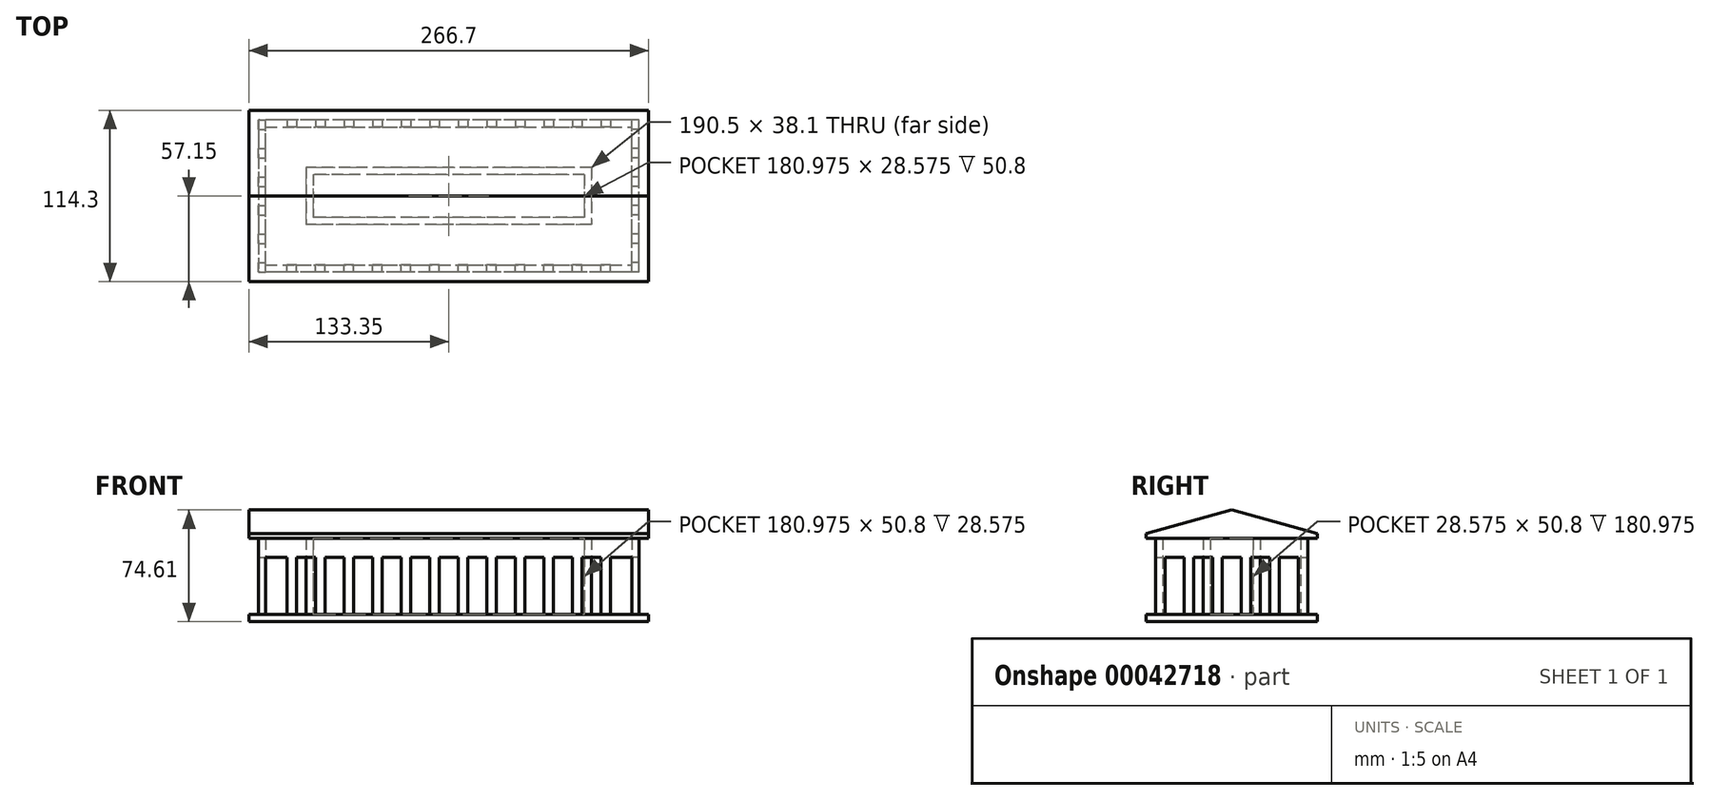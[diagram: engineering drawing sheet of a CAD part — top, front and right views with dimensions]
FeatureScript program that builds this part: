
annotation { "Feature Type Name" : "Feature", "Feature Type Description" : "" }
export const myFeature = defineFeature(function(context is Context, id is Id, definition is map)
    precondition{}
    {
        {
            var Q0;
            Q0=qCreatedBy(makeId("Top.planeOp"),FACE);
            var sketch = newSketch(context, id + "F0", { "sketchPlane" : qUnion([Q0])});
            skLineSegment(sketch, "E0.rect.bottom", {"start": v(133.35, 57.15) * mm, "end": v(-133.35, 57.15) * mm});
            skLineSegment(sketch, "E0.rect.top", {"start": v(133.35, -57.15) * mm, "end": v(-133.35, -57.15) * mm});
            skLineSegment(sketch, "E0.rect.left", {"start": v(133.35, 57.15) * mm, "end": v(133.35, -57.15) * mm});
            skLineSegment(sketch, "E0.rect.right", {"start": v(-133.35, 57.15) * mm, "end": v(-133.35, -57.15) * mm});
            skPoint(sketch, "E0.rect.middle", {"position": v(0, 0) * mm});
            skSolve(sketch);
        }
        {
            var Q0;
            Q0 = qSketchRegion(id + "F0", true);
            extrude(context, id + "F1", {"entities" : qUnion([Q0]), "depth" : 4.76 * mm});
        }
        {
            var Q0;
            Q0=makeQuery(id+"F1.opExtrude","CAP_FACE",FACE,{"disambiguationData":[OSD([sQuery(id+"F0.wireOp",EDGE,"E0.rect.bottom"),sQuery(id+"F0.wireOp",EDGE,"E0.rect.top"),sQuery(id+"F0.wireOp",EDGE,"E0.rect.left"),sQuery(id+"F0.wireOp",EDGE,"E0.rect.right")])],"isStart":false});
            var sketch = newSketch(context, id + "F2", { "sketchPlane" : qUnion([Q0])});
            skLineSegment(sketch, "E1.bottom", {"start": v(127, -50.8) * mm, "end": v(122.24, -50.8) * mm});
            skLineSegment(sketch, "E1.top", {"start": v(127, -44.45) * mm, "end": v(122.24, -44.45) * mm});
            skLineSegment(sketch, "E1.left", {"start": v(127, -50.8) * mm, "end": v(127, -44.45) * mm});
            skLineSegment(sketch, "E1.right", {"start": v(122.24, -50.8) * mm, "end": v(122.24, -44.45) * mm});
            skLineSegment(sketch, "E2.0.1.0", {"start": v(127, -25.4) * mm, "end": v(122.24, -25.4) * mm});
            skLineSegment(sketch, "E2.0.1.1", {"start": v(122.24, -31.75) * mm, "end": v(122.24, -25.4) * mm});
            skLineSegment(sketch, "E2.0.1.2", {"start": v(127, -31.75) * mm, "end": v(127, -25.4) * mm});
            skLineSegment(sketch, "E2.0.1.3", {"start": v(127, -31.75) * mm, "end": v(122.24, -31.75) * mm});
            skLineSegment(sketch, "E2.0.2.0", {"start": v(127, -6.35) * mm, "end": v(122.24, -6.35) * mm});
            skLineSegment(sketch, "E2.0.2.1", {"start": v(122.24, -12.7) * mm, "end": v(122.24, -6.35) * mm});
            skLineSegment(sketch, "E2.0.2.2", {"start": v(127, -12.7) * mm, "end": v(127, -6.35) * mm});
            skLineSegment(sketch, "E2.0.2.3", {"start": v(127, -12.7) * mm, "end": v(122.24, -12.7) * mm});
            skLineSegment(sketch, "E2.0.3.0", {"start": v(127, 12.7) * mm, "end": v(122.24, 12.7) * mm});
            skLineSegment(sketch, "E2.0.3.1", {"start": v(122.24, 6.35) * mm, "end": v(122.24, 12.7) * mm});
            skLineSegment(sketch, "E2.0.3.2", {"start": v(127, 6.35) * mm, "end": v(127, 12.7) * mm});
            skLineSegment(sketch, "E2.0.3.3", {"start": v(127, 6.35) * mm, "end": v(122.24, 6.35) * mm});
            skLineSegment(sketch, "E2.0.4.0", {"start": v(127, 31.75) * mm, "end": v(122.24, 31.75) * mm});
            skLineSegment(sketch, "E2.0.4.1", {"start": v(122.24, 25.4) * mm, "end": v(122.24, 31.75) * mm});
            skLineSegment(sketch, "E2.0.4.2", {"start": v(127, 25.4) * mm, "end": v(127, 31.75) * mm});
            skLineSegment(sketch, "E2.0.4.3", {"start": v(127, 25.4) * mm, "end": v(122.24, 25.4) * mm});
            skLineSegment(sketch, "E2.direction1", {"start": v(122.24, -44.45) * mm, "end": v(149.23, -44.45) * mm, "construction": true});
            skLineSegment(sketch, "E2.direction2", {"start": v(122.24, -44.45) * mm, "end": v(122.24, -25.4) * mm, "construction": true});
            skLineSegment(sketch, "E3.0.0.5", {"start": v(127, 50.8) * mm, "end": v(122.24, 50.8) * mm});
            skLineSegment(sketch, "E3.3.0.5", {"start": v(122.24, 44.45) * mm, "end": v(122.24, 50.8) * mm});
            skLineSegment(sketch, "E3.6.0.5", {"start": v(127, 44.45) * mm, "end": v(127, 50.8) * mm});
            skLineSegment(sketch, "E3.9.0.5", {"start": v(127, 44.45) * mm, "end": v(122.24, 44.45) * mm});
            skLineSegment(sketch, "E4.bottom", {"start": v(107.95, 50.8) * mm, "end": v(101.6, 50.8) * mm});
            skLineSegment(sketch, "E4.top", {"start": v(107.95, 46.04) * mm, "end": v(101.6, 46.04) * mm});
            skLineSegment(sketch, "E4.left", {"start": v(107.95, 50.8) * mm, "end": v(107.95, 46.04) * mm});
            skLineSegment(sketch, "E4.right", {"start": v(101.6, 50.8) * mm, "end": v(101.6, 46.04) * mm});
            skLineSegment(sketch, "E5", {"start": v(0, -57.15) * mm, "end": v(0, 57.15) * mm, "construction": true});
            skLineSegment(sketch, "E6.MirrorCS", {"start": v(-127, -44.45) * mm, "end": v(-122.24, -44.45) * mm});
            skLineSegment(sketch, "E7.MirrorCS", {"start": v(-127, -31.75) * mm, "end": v(-122.24, -31.75) * mm});
            skLineSegment(sketch, "E8.MirrorCS", {"start": v(-127, -25.4) * mm, "end": v(-122.24, -25.4) * mm});
            skLineSegment(sketch, "E9.MirrorCS", {"start": v(-127, -6.35) * mm, "end": v(-122.24, -6.35) * mm});
            skLineSegment(sketch, "E10.MirrorCS", {"start": v(-127, -31.75) * mm, "end": v(-127, -25.4) * mm});
            skLineSegment(sketch, "E11.MirrorCS", {"start": v(-122.24, -31.75) * mm, "end": v(-122.24, -25.4) * mm});
            skLineSegment(sketch, "E12.MirrorCS", {"start": v(-122.24, -50.8) * mm, "end": v(-122.24, -44.45) * mm});
            skLineSegment(sketch, "E13.MirrorCS", {"start": v(-127, -50.8) * mm, "end": v(-127, -44.45) * mm});
            skLineSegment(sketch, "E14.MirrorCS", {"start": v(-127, -50.8) * mm, "end": v(-122.24, -50.8) * mm});
            skLineSegment(sketch, "E15.MirrorCS", {"start": v(-127, 6.35) * mm, "end": v(-122.24, 6.35) * mm});
            skLineSegment(sketch, "E16.MirrorCS", {"start": v(-127, 6.35) * mm, "end": v(-127, 12.7) * mm});
            skLineSegment(sketch, "E17.MirrorCS", {"start": v(-122.24, 6.35) * mm, "end": v(-122.24, 12.7) * mm});
            skLineSegment(sketch, "E18.MirrorCS", {"start": v(-122.24, -12.7) * mm, "end": v(-122.24, -6.35) * mm});
            skLineSegment(sketch, "E19.MirrorCS", {"start": v(-127, -12.7) * mm, "end": v(-127, -6.35) * mm});
            skLineSegment(sketch, "E20.MirrorCS", {"start": v(-127, -12.7) * mm, "end": v(-122.24, -12.7) * mm});
            skLineSegment(sketch, "E21.MirrorCS", {"start": v(-122.24, 25.4) * mm, "end": v(-122.24, 31.75) * mm});
            skLineSegment(sketch, "E22.MirrorCS", {"start": v(-127, 44.45) * mm, "end": v(-127, 50.8) * mm});
            skLineSegment(sketch, "E23.MirrorCS", {"start": v(-127, 12.7) * mm, "end": v(-122.24, 12.7) * mm});
            skLineSegment(sketch, "E24.MirrorCS", {"start": v(-127, 25.4) * mm, "end": v(-122.24, 25.4) * mm});
            skLineSegment(sketch, "E25.MirrorCS", {"start": v(-127, 31.75) * mm, "end": v(-122.24, 31.75) * mm});
            skLineSegment(sketch, "E26.MirrorCS", {"start": v(-127, 25.4) * mm, "end": v(-127, 31.75) * mm});
            skLineSegment(sketch, "E27.MirrorCS", {"start": v(-127, 50.8) * mm, "end": v(-122.24, 50.8) * mm});
            skLineSegment(sketch, "E28.MirrorCS", {"start": v(-127, 44.45) * mm, "end": v(-122.24, 44.45) * mm});
            skLineSegment(sketch, "E29.MirrorCS", {"start": v(-122.24, 44.45) * mm, "end": v(-122.24, 50.8) * mm});
            skLineSegment(sketch, "E30.0.0", {"start": v(133.35, 57.15) * mm, "end": v(-133.35, 57.15) * mm});
            skLineSegment(sketch, "E30.0.2", {"start": v(-133.35, 57.15) * mm, "end": v(133.35, 57.15) * mm});
            skLineSegment(sketch, "E31.0.0", {"start": v(133.35, -57.15) * mm, "end": v(133.35, 57.15) * mm});
            skLineSegment(sketch, "E31.0.2", {"start": v(-133.35, 57.15) * mm, "end": v(-133.35, -57.15) * mm});
            skLineSegment(sketch, "E31.0.3", {"start": v(-133.35, -57.15) * mm, "end": v(133.35, -57.15) * mm});
            skLineSegment(sketch, "E32.1.0.0", {"start": v(88.9, 50.8) * mm, "end": v(82.55, 50.8) * mm});
            skLineSegment(sketch, "E32.1.0.1", {"start": v(88.9, 46.04) * mm, "end": v(82.55, 46.04) * mm});
            skLineSegment(sketch, "E32.1.0.2", {"start": v(88.9, 50.8) * mm, "end": v(88.9, 46.04) * mm});
            skLineSegment(sketch, "E32.1.0.3", {"start": v(82.55, 50.8) * mm, "end": v(82.55, 46.04) * mm});
            skLineSegment(sketch, "E32.2.0.0", {"start": v(69.85, 50.8) * mm, "end": v(63.5, 50.8) * mm});
            skLineSegment(sketch, "E32.2.0.1", {"start": v(69.85, 46.04) * mm, "end": v(63.5, 46.04) * mm});
            skLineSegment(sketch, "E32.2.0.2", {"start": v(69.85, 50.8) * mm, "end": v(69.85, 46.04) * mm});
            skLineSegment(sketch, "E32.2.0.3", {"start": v(63.5, 50.8) * mm, "end": v(63.5, 46.04) * mm});
            skLineSegment(sketch, "E32.3.0.0", {"start": v(50.8, 50.8) * mm, "end": v(44.45, 50.8) * mm});
            skLineSegment(sketch, "E32.3.0.1", {"start": v(50.8, 46.04) * mm, "end": v(44.45, 46.04) * mm});
            skLineSegment(sketch, "E32.3.0.2", {"start": v(50.8, 50.8) * mm, "end": v(50.8, 46.04) * mm});
            skLineSegment(sketch, "E32.3.0.3", {"start": v(44.45, 50.8) * mm, "end": v(44.45, 46.04) * mm});
            skLineSegment(sketch, "E32.4.0.0", {"start": v(31.75, 50.8) * mm, "end": v(25.4, 50.8) * mm});
            skLineSegment(sketch, "E32.4.0.1", {"start": v(31.75, 46.04) * mm, "end": v(25.4, 46.04) * mm});
            skLineSegment(sketch, "E32.4.0.2", {"start": v(31.75, 50.8) * mm, "end": v(31.75, 46.04) * mm});
            skLineSegment(sketch, "E32.4.0.3", {"start": v(25.4, 50.8) * mm, "end": v(25.4, 46.04) * mm});
            skLineSegment(sketch, "E32.5.0.0", {"start": v(12.7, 50.8) * mm, "end": v(6.35, 50.8) * mm});
            skLineSegment(sketch, "E32.5.0.1", {"start": v(12.7, 46.04) * mm, "end": v(6.35, 46.04) * mm});
            skLineSegment(sketch, "E32.5.0.2", {"start": v(12.7, 50.8) * mm, "end": v(12.7, 46.04) * mm});
            skLineSegment(sketch, "E32.5.0.3", {"start": v(6.35, 50.8) * mm, "end": v(6.35, 46.04) * mm});
            skLineSegment(sketch, "E32.6.0.0", {"start": v(-6.35, 50.8) * mm, "end": v(-12.7, 50.8) * mm});
            skLineSegment(sketch, "E32.6.0.1", {"start": v(-6.35, 46.04) * mm, "end": v(-12.7, 46.04) * mm});
            skLineSegment(sketch, "E32.6.0.2", {"start": v(-6.35, 50.8) * mm, "end": v(-6.35, 46.04) * mm});
            skLineSegment(sketch, "E32.6.0.3", {"start": v(-12.7, 50.8) * mm, "end": v(-12.7, 46.04) * mm});
            skLineSegment(sketch, "E32.7.0.0", {"start": v(-25.4, 50.8) * mm, "end": v(-31.75, 50.8) * mm});
            skLineSegment(sketch, "E32.7.0.1", {"start": v(-25.4, 46.04) * mm, "end": v(-31.75, 46.04) * mm});
            skLineSegment(sketch, "E32.7.0.2", {"start": v(-25.4, 50.8) * mm, "end": v(-25.4, 46.04) * mm});
            skLineSegment(sketch, "E32.7.0.3", {"start": v(-31.75, 50.8) * mm, "end": v(-31.75, 46.04) * mm});
            skLineSegment(sketch, "E32.8.0.0", {"start": v(-44.45, 50.8) * mm, "end": v(-50.8, 50.8) * mm});
            skLineSegment(sketch, "E32.8.0.1", {"start": v(-44.45, 46.04) * mm, "end": v(-50.8, 46.04) * mm});
            skLineSegment(sketch, "E32.8.0.2", {"start": v(-44.45, 50.8) * mm, "end": v(-44.45, 46.04) * mm});
            skLineSegment(sketch, "E32.8.0.3", {"start": v(-50.8, 50.8) * mm, "end": v(-50.8, 46.04) * mm});
            skLineSegment(sketch, "E32.9.0.0", {"start": v(-63.5, 50.8) * mm, "end": v(-69.85, 50.8) * mm});
            skLineSegment(sketch, "E32.9.0.1", {"start": v(-63.5, 46.04) * mm, "end": v(-69.85, 46.04) * mm});
            skLineSegment(sketch, "E32.9.0.2", {"start": v(-63.5, 50.8) * mm, "end": v(-63.5, 46.04) * mm});
            skLineSegment(sketch, "E32.9.0.3", {"start": v(-69.85, 50.8) * mm, "end": v(-69.85, 46.04) * mm});
            skLineSegment(sketch, "E32.10.0.0", {"start": v(-82.55, 50.8) * mm, "end": v(-88.9, 50.8) * mm});
            skLineSegment(sketch, "E32.10.0.1", {"start": v(-82.55, 46.04) * mm, "end": v(-88.9, 46.04) * mm});
            skLineSegment(sketch, "E32.10.0.2", {"start": v(-82.55, 50.8) * mm, "end": v(-82.55, 46.04) * mm});
            skLineSegment(sketch, "E32.10.0.3", {"start": v(-88.9, 50.8) * mm, "end": v(-88.9, 46.04) * mm});
            skLineSegment(sketch, "E32.direction1", {"start": v(101.6, 50.8) * mm, "end": v(82.55, 50.8) * mm, "construction": true});
            skLineSegment(sketch, "E33.0.11.0", {"start": v(-101.6, 50.8) * mm, "end": v(-107.95, 50.8) * mm});
            skLineSegment(sketch, "E33.3.11.0", {"start": v(-101.6, 46.04) * mm, "end": v(-107.95, 46.04) * mm});
            skLineSegment(sketch, "E33.6.11.0", {"start": v(-101.6, 50.8) * mm, "end": v(-101.6, 46.04) * mm});
            skLineSegment(sketch, "E33.9.11.0", {"start": v(-107.95, 50.8) * mm, "end": v(-107.95, 46.04) * mm});
            skLineSegment(sketch, "E34", {"start": v(133.35, 0) * mm, "end": v(-133.35, 0) * mm, "construction": true});
            skLineSegment(sketch, "E35.MirrorCS", {"start": v(107.95, -50.8) * mm, "end": v(107.95, -46.04) * mm});
            skLineSegment(sketch, "E36.MirrorCS", {"start": v(107.95, -46.04) * mm, "end": v(101.6, -46.04) * mm});
            skLineSegment(sketch, "E37.MirrorCS", {"start": v(107.95, -50.8) * mm, "end": v(101.6, -50.8) * mm});
            skLineSegment(sketch, "E38.MirrorCS", {"start": v(101.6, -50.8) * mm, "end": v(101.6, -46.04) * mm});
            skLineSegment(sketch, "E39.MirrorCS", {"start": v(88.9, -50.8) * mm, "end": v(88.9, -46.04) * mm});
            skLineSegment(sketch, "E40.MirrorCS", {"start": v(88.9, -46.04) * mm, "end": v(82.55, -46.04) * mm});
            skLineSegment(sketch, "E41.MirrorCS", {"start": v(82.55, -50.8) * mm, "end": v(82.55, -46.04) * mm});
            skLineSegment(sketch, "E42.MirrorCS", {"start": v(88.9, -50.8) * mm, "end": v(82.55, -50.8) * mm});
            skLineSegment(sketch, "E43.MirrorCS", {"start": v(69.85, -50.8) * mm, "end": v(69.85, -46.04) * mm});
            skLineSegment(sketch, "E44.MirrorCS", {"start": v(-6.35, -50.8) * mm, "end": v(-6.35, -46.04) * mm});
            skLineSegment(sketch, "E45.MirrorCS", {"start": v(-82.55, -50.8) * mm, "end": v(-82.55, -46.04) * mm});
            skLineSegment(sketch, "E46.MirrorCS", {"start": v(-44.45, -46.04) * mm, "end": v(-50.8, -46.04) * mm});
            skLineSegment(sketch, "E47.MirrorCS", {"start": v(31.75, -46.04) * mm, "end": v(25.4, -46.04) * mm});
            skLineSegment(sketch, "E48.MirrorCS", {"start": v(69.85, -46.04) * mm, "end": v(63.5, -46.04) * mm});
            skLineSegment(sketch, "E49.MirrorCS", {"start": v(-6.35, -46.04) * mm, "end": v(-12.7, -46.04) * mm});
            skLineSegment(sketch, "E50.MirrorCS", {"start": v(-82.55, -46.04) * mm, "end": v(-88.9, -46.04) * mm});
            skLineSegment(sketch, "E51.MirrorCS", {"start": v(-44.45, -50.8) * mm, "end": v(-50.8, -50.8) * mm});
            skLineSegment(sketch, "E52.MirrorCS", {"start": v(-107.95, -50.8) * mm, "end": v(-107.95, -46.04) * mm});
            skLineSegment(sketch, "E53.MirrorCS", {"start": v(31.75, -50.8) * mm, "end": v(25.4, -50.8) * mm});
            skLineSegment(sketch, "E54.MirrorCS", {"start": v(69.85, -50.8) * mm, "end": v(63.5, -50.8) * mm});
            skLineSegment(sketch, "E55.MirrorCS", {"start": v(-6.35, -50.8) * mm, "end": v(-12.7, -50.8) * mm});
            skLineSegment(sketch, "E56.MirrorCS", {"start": v(-82.55, -50.8) * mm, "end": v(-88.9, -50.8) * mm});
            skLineSegment(sketch, "E57.MirrorCS", {"start": v(-31.75, -50.8) * mm, "end": v(-31.75, -46.04) * mm});
            skLineSegment(sketch, "E58.MirrorCS", {"start": v(-101.6, -50.8) * mm, "end": v(-101.6, -46.04) * mm});
            skLineSegment(sketch, "E59.MirrorCS", {"start": v(44.45, -50.8) * mm, "end": v(44.45, -46.04) * mm});
            skLineSegment(sketch, "E60.MirrorCS", {"start": v(-25.4, -50.8) * mm, "end": v(-25.4, -46.04) * mm});
            skLineSegment(sketch, "E61.MirrorCS", {"start": v(-101.6, -46.04) * mm, "end": v(-107.95, -46.04) * mm});
            skLineSegment(sketch, "E62.MirrorCS", {"start": v(50.8, -50.8) * mm, "end": v(50.8, -46.04) * mm});
            skLineSegment(sketch, "E63.MirrorCS", {"start": v(6.35, -50.8) * mm, "end": v(6.35, -46.04) * mm});
            skLineSegment(sketch, "E64.MirrorCS", {"start": v(-69.85, -50.8) * mm, "end": v(-69.85, -46.04) * mm});
            skLineSegment(sketch, "E65.MirrorCS", {"start": v(50.8, -46.04) * mm, "end": v(44.45, -46.04) * mm});
            skLineSegment(sketch, "E66.MirrorCS", {"start": v(-25.4, -46.04) * mm, "end": v(-31.75, -46.04) * mm});
            skLineSegment(sketch, "E67.MirrorCS", {"start": v(12.7, -50.8) * mm, "end": v(12.7, -46.04) * mm});
            skLineSegment(sketch, "E68.MirrorCS", {"start": v(-63.5, -50.8) * mm, "end": v(-63.5, -46.04) * mm});
            skLineSegment(sketch, "E69.MirrorCS", {"start": v(-101.6, -50.8) * mm, "end": v(-107.95, -50.8) * mm});
            skLineSegment(sketch, "E70.MirrorCS", {"start": v(50.8, -50.8) * mm, "end": v(44.45, -50.8) * mm});
            skLineSegment(sketch, "E71.MirrorCS", {"start": v(12.7, -46.04) * mm, "end": v(6.35, -46.04) * mm});
            skLineSegment(sketch, "E72.MirrorCS", {"start": v(-25.4, -50.8) * mm, "end": v(-31.75, -50.8) * mm});
            skLineSegment(sketch, "E73.MirrorCS", {"start": v(-63.5, -46.04) * mm, "end": v(-69.85, -46.04) * mm});
            skLineSegment(sketch, "E74.MirrorCS", {"start": v(-50.8, -50.8) * mm, "end": v(-50.8, -46.04) * mm});
            skLineSegment(sketch, "E75.MirrorCS", {"start": v(25.4, -50.8) * mm, "end": v(25.4, -46.04) * mm});
            skLineSegment(sketch, "E76.MirrorCS", {"start": v(63.5, -50.8) * mm, "end": v(63.5, -46.04) * mm});
            skLineSegment(sketch, "E77.MirrorCS", {"start": v(-12.7, -50.8) * mm, "end": v(-12.7, -46.04) * mm});
            skLineSegment(sketch, "E78.MirrorCS", {"start": v(-63.5, -50.8) * mm, "end": v(-69.85, -50.8) * mm});
            skLineSegment(sketch, "E79.MirrorCS", {"start": v(12.7, -50.8) * mm, "end": v(6.35, -50.8) * mm});
            skLineSegment(sketch, "E80.MirrorCS", {"start": v(31.75, -50.8) * mm, "end": v(31.75, -46.04) * mm});
            skLineSegment(sketch, "E81.MirrorCS", {"start": v(-88.9, -50.8) * mm, "end": v(-88.9, -46.04) * mm});
            skLineSegment(sketch, "E82.MirrorCS", {"start": v(-44.45, -50.8) * mm, "end": v(-44.45, -46.04) * mm});
            skSolve(sketch);
        }
        {
            var Q0;
            Q0=makeQuery(id+"F2.imprint","IMPRINT",FACE,{"disambiguationData":[TD([[makeQuery(id+"F2.imprint","IMPRINT",EDGE,{"derivedFrom":sQuery(id+"F2.wireOp",EDGE,"E1.bottom")}),-1.0]])]});
            var Q1;
            Q1=makeQuery(id+"F2.imprint","IMPRINT",FACE,{"disambiguationData":[TD([[makeQuery(id+"F2.imprint","IMPRINT",EDGE,{"derivedFrom":sQuery(id+"F2.wireOp",EDGE,"E2.0.3.0")}),1.0]])]});
            var Q2;
            {var subQ5=sQuery(id+"F2.wireOp",EDGE,"E2.0.4.0");Q2=makeQuery(id+"F2.imprint","IMPRINT",FACE,{"disambiguationData":[TD([[makeQuery(id+"F2.imprint","IMPRINT",EDGE,{"derivedFrom":subQ5}),1.0]])]});}
            var Q3;
            {var subQ5=sQuery(id+"F2.wireOp",EDGE,"E2.0.4.3");Q3=makeQuery(id+"F2.imprint","IMPRINT",FACE,{"disambiguationData":[TD([[makeQuery(id+"F2.imprint","IMPRINT",EDGE,{"derivedFrom":subQ5}),-1.0]])]});}
            var Q4;
            Q4=makeQuery(id+"F2.imprint","IMPRINT",FACE,{"disambiguationData":[TD([[makeQuery(id+"F2.imprint","IMPRINT",EDGE,{"derivedFrom":sQuery(id+"F2.wireOp",EDGE,"E2.0.2.0")}),1.0]])]});
            var Q5;
            Q5=makeQuery(id+"F2.imprint","IMPRINT",FACE,{"disambiguationData":[TD([[makeQuery(id+"F2.imprint","IMPRINT",EDGE,{"derivedFrom":sQuery(id+"F2.wireOp",EDGE,"E2.0.1.0")}),1.0]])]});
            var Q6;
            Q6=makeQuery(id+"F2.imprint","IMPRINT",FACE,{"disambiguationData":[TD([[makeQuery(id+"F2.imprint","IMPRINT",EDGE,{"derivedFrom":sQuery(id+"F2.wireOp",EDGE,"E22.MirrorCS")}),-1.0]])]});
            var Q7;
            Q7=makeQuery(id+"F2.imprint","IMPRINT",FACE,{"disambiguationData":[TD([[makeQuery(id+"F2.imprint","IMPRINT",EDGE,{"derivedFrom":sQuery(id+"F2.wireOp",EDGE,"E33.0.11.0")}),1.0]])]});
            var Q8;
            Q8=makeQuery(id+"F2.imprint","IMPRINT",FACE,{"disambiguationData":[TD([[makeQuery(id+"F2.imprint","IMPRINT",EDGE,{"derivedFrom":sQuery(id+"F2.wireOp",EDGE,"E32.10.0.0")}),1.0]])]});
            var Q9;
            Q9=makeQuery(id+"F2.imprint","IMPRINT",FACE,{"disambiguationData":[TD([[makeQuery(id+"F2.imprint","IMPRINT",EDGE,{"derivedFrom":sQuery(id+"F2.wireOp",EDGE,"E32.9.0.0")}),1.0]])]});
            var Q10;
            Q10=makeQuery(id+"F2.imprint","IMPRINT",FACE,{"disambiguationData":[TD([[makeQuery(id+"F2.imprint","IMPRINT",EDGE,{"derivedFrom":sQuery(id+"F2.wireOp",EDGE,"E32.8.0.0")}),1.0]])]});
            var Q11;
            Q11=makeQuery(id+"F2.imprint","IMPRINT",FACE,{"disambiguationData":[TD([[makeQuery(id+"F2.imprint","IMPRINT",EDGE,{"derivedFrom":sQuery(id+"F2.wireOp",EDGE,"E32.7.0.0")}),1.0]])]});
            var Q12;
            Q12=makeQuery(id+"F2.imprint","IMPRINT",FACE,{"disambiguationData":[TD([[makeQuery(id+"F2.imprint","IMPRINT",EDGE,{"derivedFrom":sQuery(id+"F2.wireOp",EDGE,"E32.5.0.0")}),1.0]])]});
            var Q13;
            Q13=makeQuery(id+"F2.imprint","IMPRINT",FACE,{"disambiguationData":[TD([[makeQuery(id+"F2.imprint","IMPRINT",EDGE,{"derivedFrom":sQuery(id+"F2.wireOp",EDGE,"E32.4.0.0")}),1.0]])]});
            var Q14;
            Q14=makeQuery(id+"F2.imprint","IMPRINT",FACE,{"disambiguationData":[TD([[makeQuery(id+"F2.imprint","IMPRINT",EDGE,{"derivedFrom":sQuery(id+"F2.wireOp",EDGE,"E32.3.0.0")}),1.0]])]});
            var Q15;
            Q15=makeQuery(id+"F2.imprint","IMPRINT",FACE,{"disambiguationData":[TD([[makeQuery(id+"F2.imprint","IMPRINT",EDGE,{"derivedFrom":sQuery(id+"F2.wireOp",EDGE,"E32.2.0.0")}),1.0]])]});
            var Q16;
            Q16=makeQuery(id+"F2.imprint","IMPRINT",FACE,{"disambiguationData":[TD([[makeQuery(id+"F2.imprint","IMPRINT",EDGE,{"derivedFrom":sQuery(id+"F2.wireOp",EDGE,"E32.1.0.0")}),1.0]])]});
            var Q17;
            Q17=makeQuery(id+"F2.imprint","IMPRINT",FACE,{"disambiguationData":[TD([[makeQuery(id+"F2.imprint","IMPRINT",EDGE,{"derivedFrom":sQuery(id+"F2.wireOp",EDGE,"E4.bottom")}),1.0]])]});
            var Q18;
            Q18=makeQuery(id+"F2.imprint","IMPRINT",FACE,{"disambiguationData":[TD([[makeQuery(id+"F2.imprint","IMPRINT",EDGE,{"derivedFrom":sQuery(id+"F2.wireOp",EDGE,"E3.0.0.5")}),1.0]])]});
            var Q19;
            Q19=makeQuery(id+"F2.imprint","IMPRINT",FACE,{"disambiguationData":[TD([[makeQuery(id+"F2.imprint","IMPRINT",EDGE,{"derivedFrom":sQuery(id+"F2.wireOp",EDGE,"E32.6.0.0")}),1.0]])]});
            var Q20;
            Q20=makeQuery(id+"F2.imprint","IMPRINT",FACE,{"disambiguationData":[TD([[makeQuery(id+"F2.imprint","IMPRINT",EDGE,{"derivedFrom":sQuery(id+"F2.wireOp",EDGE,"E21.MirrorCS")}),1.0]])]});
            var Q21;
            Q21=makeQuery(id+"F2.imprint","IMPRINT",FACE,{"disambiguationData":[TD([[makeQuery(id+"F2.imprint","IMPRINT",EDGE,{"derivedFrom":sQuery(id+"F2.wireOp",EDGE,"E15.MirrorCS")}),1.0]])]});
            var Q22;
            Q22=makeQuery(id+"F2.imprint","IMPRINT",FACE,{"disambiguationData":[TD([[makeQuery(id+"F2.imprint","IMPRINT",EDGE,{"derivedFrom":sQuery(id+"F2.wireOp",EDGE,"E9.MirrorCS")}),-1.0]])]});
            var Q23;
            Q23=makeQuery(id+"F2.imprint","IMPRINT",FACE,{"disambiguationData":[TD([[makeQuery(id+"F2.imprint","IMPRINT",EDGE,{"derivedFrom":sQuery(id+"F2.wireOp",EDGE,"E6.MirrorCS")}),-1.0]])]});
            var Q24;
            Q24=makeQuery(id+"F2.imprint","IMPRINT",FACE,{"disambiguationData":[TD([[makeQuery(id+"F2.imprint","IMPRINT",EDGE,{"derivedFrom":sQuery(id+"F2.wireOp",EDGE,"E52.MirrorCS")}),-1.0]])]});
            var Q25;
            Q25=makeQuery(id+"F2.imprint","IMPRINT",FACE,{"disambiguationData":[TD([[makeQuery(id+"F2.imprint","IMPRINT",EDGE,{"derivedFrom":sQuery(id+"F2.wireOp",EDGE,"E45.MirrorCS")}),1.0]])]});
            var Q26;
            Q26=makeQuery(id+"F2.imprint","IMPRINT",FACE,{"disambiguationData":[TD([[makeQuery(id+"F2.imprint","IMPRINT",EDGE,{"derivedFrom":sQuery(id+"F2.wireOp",EDGE,"E7.MirrorCS")}),1.0]])]});
            var Q27;
            Q27=makeQuery(id+"F2.imprint","IMPRINT",FACE,{"disambiguationData":[TD([[makeQuery(id+"F2.imprint","IMPRINT",EDGE,{"derivedFrom":sQuery(id+"F2.wireOp",EDGE,"E64.MirrorCS")}),-1.0]])]});
            var Q28;
            Q28=makeQuery(id+"F2.imprint","IMPRINT",FACE,{"disambiguationData":[TD([[makeQuery(id+"F2.imprint","IMPRINT",EDGE,{"derivedFrom":sQuery(id+"F2.wireOp",EDGE,"E46.MirrorCS")}),1.0]])]});
            var Q29;
            Q29=makeQuery(id+"F2.imprint","IMPRINT",FACE,{"disambiguationData":[TD([[makeQuery(id+"F2.imprint","IMPRINT",EDGE,{"derivedFrom":sQuery(id+"F2.wireOp",EDGE,"E57.MirrorCS")}),-1.0]])]});
            var Q30;
            Q30=makeQuery(id+"F2.imprint","IMPRINT",FACE,{"disambiguationData":[TD([[makeQuery(id+"F2.imprint","IMPRINT",EDGE,{"derivedFrom":sQuery(id+"F2.wireOp",EDGE,"E44.MirrorCS")}),1.0]])]});
            var Q31;
            Q31=makeQuery(id+"F2.imprint","IMPRINT",FACE,{"disambiguationData":[TD([[makeQuery(id+"F2.imprint","IMPRINT",EDGE,{"derivedFrom":sQuery(id+"F2.wireOp",EDGE,"E63.MirrorCS")}),-1.0]])]});
            var Q32;
            Q32=makeQuery(id+"F2.imprint","IMPRINT",FACE,{"disambiguationData":[TD([[makeQuery(id+"F2.imprint","IMPRINT",EDGE,{"derivedFrom":sQuery(id+"F2.wireOp",EDGE,"E47.MirrorCS")}),1.0]])]});
            var Q33;
            Q33=makeQuery(id+"F2.imprint","IMPRINT",FACE,{"disambiguationData":[TD([[makeQuery(id+"F2.imprint","IMPRINT",EDGE,{"derivedFrom":sQuery(id+"F2.wireOp",EDGE,"E59.MirrorCS")}),-1.0]])]});
            var Q34;
            Q34=makeQuery(id+"F2.imprint","IMPRINT",FACE,{"disambiguationData":[TD([[makeQuery(id+"F2.imprint","IMPRINT",EDGE,{"derivedFrom":sQuery(id+"F2.wireOp",EDGE,"E43.MirrorCS")}),1.0]])]});
            var Q35;
            Q35=makeQuery(id+"F2.imprint","IMPRINT",FACE,{"disambiguationData":[TD([[makeQuery(id+"F2.imprint","IMPRINT",EDGE,{"derivedFrom":sQuery(id+"F2.wireOp",EDGE,"E39.MirrorCS")}),1.0]])]});
            var Q36;
            Q36=makeQuery(id+"F2.imprint","IMPRINT",FACE,{"disambiguationData":[TD([[makeQuery(id+"F2.imprint","IMPRINT",EDGE,{"derivedFrom":sQuery(id+"F2.wireOp",EDGE,"E35.MirrorCS")}),1.0]])]});
            extrude(context, id + "F3", {"entities" : qUnion([Q0, Q1, Q2, Q3, Q4, Q5, Q6, Q7, Q8, Q9, Q10, Q11, Q12, Q13, Q14, Q15, Q16, Q17, Q18, Q19, Q20, Q21, Q22, Q23, Q24, Q25, Q26, Q27, Q28, Q29, Q30, Q31, Q32, Q33, Q34, Q35, Q36]), "operationType" : NewBodyOperationType.ADD, "depth" : 38.1 * mm});
        }
        {
            var Q0;
            Q0=makeQuery(id+"F3.opExtrude","CAP_FACE",FACE,{"disambiguationData":[OSD([sQuery(id+"F2.wireOp",EDGE,"E3.0.0.5"),sQuery(id+"F2.wireOp",EDGE,"E3.3.0.5"),sQuery(id+"F2.wireOp",EDGE,"E3.6.0.5"),sQuery(id+"F2.wireOp",EDGE,"E3.9.0.5")])],"isStart":false});
            var sketch = newSketch(context, id + "F4", { "sketchPlane" : qUnion([Q0])});
            skPoint(sketch, "E83.0", {"position": v(-127, -50.8) * mm});
            skLineSegment(sketch, "E84.bottom", {"start": v(127, 50.8) * mm, "end": v(-127, 50.8) * mm});
            skLineSegment(sketch, "E84.top", {"start": v(127, -50.8) * mm, "end": v(-127, -50.8) * mm});
            skLineSegment(sketch, "E84.left", {"start": v(127, 50.8) * mm, "end": v(127, -50.8) * mm});
            skLineSegment(sketch, "E84.right", {"start": v(-127, 50.8) * mm, "end": v(-127, -50.8) * mm});
            skPoint(sketch, "E85.0", {"position": v(-107.95, -46.04) * mm});
            skPoint(sketch, "E86.0", {"position": v(107.95, 46.04) * mm});
            skLineSegment(sketch, "E87.0", {"start": v(-122.24, -50.8) * mm, "end": v(-122.24, -44.45) * mm});
            skLineSegment(sketch, "E88.0", {"start": v(122.24, 44.45) * mm, "end": v(122.24, 50.8) * mm});
            skLineSegment(sketch, "E89.bottom", {"start": v(-122.24, -46.04) * mm, "end": v(122.24, -46.04) * mm});
            skLineSegment(sketch, "E89.top", {"start": v(-122.24, 46.04) * mm, "end": v(122.24, 46.04) * mm});
            skLineSegment(sketch, "E89.left", {"start": v(-122.24, -46.04) * mm, "end": v(-122.24, 46.04) * mm});
            skLineSegment(sketch, "E89.right", {"start": v(122.24, -46.04) * mm, "end": v(122.24, 46.04) * mm});
            skSolve(sketch);
        }
        {
            var Q0;
            Q0 = qSketchRegion(id + "F4", true);
            extrude(context, id + "F5", {"entities" : qUnion([Q0]), "operationType" : NewBodyOperationType.ADD, "depth" : 12.7 * mm});
        }
        {
            var Q0;
            Q0=makeQuery(id+"F1.opExtrude","CAP_FACE",FACE,{"disambiguationData":[OSD([sQuery(id+"F0.wireOp",EDGE,"E0.rect.bottom"),sQuery(id+"F0.wireOp",EDGE,"E0.rect.top"),sQuery(id+"F0.wireOp",EDGE,"E0.rect.left"),sQuery(id+"F0.wireOp",EDGE,"E0.rect.right")])],"isStart":false});
            var sketch = newSketch(context, id + "F6", { "sketchPlane" : qUnion([Q0])});
            skLineSegment(sketch, "E90.0", {"start": v(95.25, 19.05) * mm, "end": v(-95.25, 19.05) * mm});
            skLineSegment(sketch, "E90.1", {"start": v(95.25, 19.05) * mm, "end": v(95.25, -19.05) * mm});
            skLineSegment(sketch, "E90.2", {"start": v(95.25, -19.05) * mm, "end": v(-95.25, -19.05) * mm});
            skLineSegment(sketch, "E90.3", {"start": v(-95.25, 19.05) * mm, "end": v(-95.25, -19.05) * mm});
            skLineSegment(sketch, "E91.0", {"start": v(127, -50.8) * mm, "end": v(127, 50.8) * mm});
            skLineSegment(sketch, "E91.1", {"start": v(-127, -50.8) * mm, "end": v(127, -50.8) * mm});
            skLineSegment(sketch, "E91.2", {"start": v(-127, 50.8) * mm, "end": v(-127, -50.8) * mm});
            skLineSegment(sketch, "E91.3", {"start": v(127, 50.8) * mm, "end": v(-127, 50.8) * mm});
            skLineSegment(sketch, "E92.0", {"start": v(90.49, 14.29) * mm, "end": v(-90.49, 14.29) * mm});
            skLineSegment(sketch, "E92.1", {"start": v(90.49, 14.29) * mm, "end": v(90.49, -14.29) * mm});
            skLineSegment(sketch, "E92.2", {"start": v(90.49, -14.29) * mm, "end": v(-90.49, -14.29) * mm});
            skLineSegment(sketch, "E92.3", {"start": v(-90.49, 14.29) * mm, "end": v(-90.49, -14.29) * mm});
            skSolve(sketch);
        }
        {
            var Q0;
            {var subQ0=makeQuery(id+"F3.opExtrude","CAP_EDGE",EDGE,{"disambiguationData":[OSD([sQuery(id+"F2.wireOp",EDGE,"E2.0.4.0")])],"isStart":true});Q0=makeQuery(id+"F6.imprint","IMPRINT",FACE,{"disambiguationData":[TD([[makeQuery(id+"F6.imprint","IMPRINT",EDGE,{"derivedFrom":subQ0}),1.0]])]});}
            var Q1;
            {var subQ1=makeQuery(id+"F3.opExtrude","CAP_EDGE",EDGE,{"disambiguationData":[OSD([sQuery(id+"F2.wireOp",EDGE,"E2.0.3.0")])],"isStart":true});Q1=makeQuery(id+"F6.imprint","IMPRINT",FACE,{"disambiguationData":[TD([[makeQuery(id+"F6.imprint","IMPRINT",EDGE,{"derivedFrom":subQ1}),1.0]])]});}
            var Q2;
            {var subQ0=makeQuery(id+"F3.opExtrude","CAP_EDGE",EDGE,{"disambiguationData":[OSD([sQuery(id+"F2.wireOp",EDGE,"E2.0.2.0")])],"isStart":true});Q2=makeQuery(id+"F6.imprint","IMPRINT",FACE,{"disambiguationData":[TD([[makeQuery(id+"F6.imprint","IMPRINT",EDGE,{"derivedFrom":subQ0}),1.0]])]});}
            var Q3;
            {var subQ1=makeQuery(id+"F3.opExtrude","CAP_EDGE",EDGE,{"disambiguationData":[OSD([sQuery(id+"F2.wireOp",EDGE,"E2.0.1.0")])],"isStart":true});Q3=makeQuery(id+"F6.imprint","IMPRINT",FACE,{"disambiguationData":[TD([[makeQuery(id+"F6.imprint","IMPRINT",EDGE,{"derivedFrom":subQ1}),1.0]])]});}
            var Q4;
            {var subQ0=makeQuery(id+"F3.opExtrude","CAP_EDGE",EDGE,{"disambiguationData":[OSD([sQuery(id+"F2.wireOp",EDGE,"E3.3.0.5")])],"isStart":true});Q4=makeQuery(id+"F6.imprint","IMPRINT",FACE,{"disambiguationData":[TD([[makeQuery(id+"F6.imprint","IMPRINT",EDGE,{"derivedFrom":subQ0}),-1.0]])]});}
            var Q5;
            {var subQ0=makeQuery(id+"F3.opExtrude","CAP_EDGE",EDGE,{"disambiguationData":[OSD([sQuery(id+"F2.wireOp",EDGE,"E1.top")])],"isStart":true});Q5=makeQuery(id+"F6.imprint","IMPRINT",FACE,{"disambiguationData":[TD([[makeQuery(id+"F6.imprint","IMPRINT",EDGE,{"derivedFrom":subQ0}),1.0]])]});}
            var Q6;
            {var subQ0=makeQuery(id+"F3.opExtrude","CAP_EDGE",EDGE,{"disambiguationData":[OSD([sQuery(id+"F2.wireOp",EDGE,"E6.MirrorCS")])],"isStart":true});Q6=makeQuery(id+"F6.imprint","IMPRINT",FACE,{"disambiguationData":[TD([[makeQuery(id+"F6.imprint","IMPRINT",EDGE,{"derivedFrom":subQ0}),-1.0]])]});}
            var Q7;
            {var subQ1=makeQuery(id+"F3.opExtrude","CAP_EDGE",EDGE,{"disambiguationData":[OSD([sQuery(id+"F2.wireOp",EDGE,"E63.MirrorCS")])],"isStart":true});Q7=makeQuery(id+"F6.imprint","IMPRINT",FACE,{"disambiguationData":[TD([[makeQuery(id+"F6.imprint","IMPRINT",EDGE,{"derivedFrom":subQ1}),-1.0]])]});}
            var Q8;
            {var subQ1=makeQuery(id+"F3.opExtrude","CAP_EDGE",EDGE,{"disambiguationData":[OSD([sQuery(id+"F2.wireOp",EDGE,"E64.MirrorCS")])],"isStart":true});Q8=makeQuery(id+"F6.imprint","IMPRINT",FACE,{"disambiguationData":[TD([[makeQuery(id+"F6.imprint","IMPRINT",EDGE,{"derivedFrom":subQ1}),-1.0]])]});}
            var Q9;
            {var subQ1=makeQuery(id+"F3.opExtrude","CAP_EDGE",EDGE,{"disambiguationData":[OSD([sQuery(id+"F2.wireOp",EDGE,"E59.MirrorCS")])],"isStart":true});Q9=makeQuery(id+"F6.imprint","IMPRINT",FACE,{"disambiguationData":[TD([[makeQuery(id+"F6.imprint","IMPRINT",EDGE,{"derivedFrom":subQ1}),-1.0]])]});}
            var Q10;
            {var subQ1=makeQuery(id+"F3.opExtrude","CAP_EDGE",EDGE,{"disambiguationData":[OSD([sQuery(id+"F2.wireOp",EDGE,"E57.MirrorCS")])],"isStart":true});Q10=makeQuery(id+"F6.imprint","IMPRINT",FACE,{"disambiguationData":[TD([[makeQuery(id+"F6.imprint","IMPRINT",EDGE,{"derivedFrom":subQ1}),-1.0]])]});}
            var Q11;
            {var subQ1=makeQuery(id+"F3.opExtrude","CAP_EDGE",EDGE,{"disambiguationData":[OSD([sQuery(id+"F2.wireOp",EDGE,"E52.MirrorCS")])],"isStart":true});Q11=makeQuery(id+"F6.imprint","IMPRINT",FACE,{"disambiguationData":[TD([[makeQuery(id+"F6.imprint","IMPRINT",EDGE,{"derivedFrom":subQ1}),-1.0]])]});}
            var Q12;
            {var subQ0=makeQuery(id+"F3.opExtrude","CAP_EDGE",EDGE,{"disambiguationData":[OSD([sQuery(id+"F2.wireOp",EDGE,"E45.MirrorCS")])],"isStart":true});Q12=makeQuery(id+"F6.imprint","IMPRINT",FACE,{"disambiguationData":[TD([[makeQuery(id+"F6.imprint","IMPRINT",EDGE,{"derivedFrom":subQ0}),1.0]])]});}
            var Q13;
            {var subQ0=makeQuery(id+"F3.opExtrude","CAP_EDGE",EDGE,{"disambiguationData":[OSD([sQuery(id+"F2.wireOp",EDGE,"E44.MirrorCS")])],"isStart":true});Q13=makeQuery(id+"F6.imprint","IMPRINT",FACE,{"disambiguationData":[TD([[makeQuery(id+"F6.imprint","IMPRINT",EDGE,{"derivedFrom":subQ0}),1.0]])]});}
            var Q14;
            {var subQ0=makeQuery(id+"F3.opExtrude","CAP_EDGE",EDGE,{"disambiguationData":[OSD([sQuery(id+"F2.wireOp",EDGE,"E43.MirrorCS")])],"isStart":true});Q14=makeQuery(id+"F6.imprint","IMPRINT",FACE,{"disambiguationData":[TD([[makeQuery(id+"F6.imprint","IMPRINT",EDGE,{"derivedFrom":subQ0}),1.0]])]});}
            var Q15;
            {var subQ1=makeQuery(id+"F3.opExtrude","CAP_EDGE",EDGE,{"disambiguationData":[OSD([sQuery(id+"F2.wireOp",EDGE,"E39.MirrorCS")])],"isStart":true});Q15=makeQuery(id+"F6.imprint","IMPRINT",FACE,{"disambiguationData":[TD([[makeQuery(id+"F6.imprint","IMPRINT",EDGE,{"derivedFrom":subQ1}),1.0]])]});}
            var Q16;
            {var subQ1=makeQuery(id+"F3.opExtrude","CAP_EDGE",EDGE,{"disambiguationData":[OSD([sQuery(id+"F2.wireOp",EDGE,"E35.MirrorCS")])],"isStart":true});Q16=makeQuery(id+"F6.imprint","IMPRINT",FACE,{"disambiguationData":[TD([[makeQuery(id+"F6.imprint","IMPRINT",EDGE,{"derivedFrom":subQ1}),1.0]])]});}
            var Q17;
            Q17=makeQuery(id+"F6.imprint","IMPRINT",FACE,{"disambiguationData":[TD([[makeQuery(id+"F6.imprint","IMPRINT",EDGE,{"derivedFrom":makeQuery(id+"F3.opExtrude","CAP_EDGE",EDGE,{"disambiguationData":[OSD([sQuery(id+"F2.wireOp",EDGE,"E46.MirrorCS")])],"isStart":true})}),1.0]])]});
            var Q18;
            Q18=makeQuery(id+"F6.imprint","IMPRINT",FACE,{"disambiguationData":[TD([[makeQuery(id+"F6.imprint","IMPRINT",EDGE,{"derivedFrom":makeQuery(id+"F3.opExtrude","CAP_EDGE",EDGE,{"disambiguationData":[OSD([sQuery(id+"F2.wireOp",EDGE,"E47.MirrorCS")])],"isStart":true})}),1.0]])]});
            var Q19;
            Q19=makeQuery(id+"F6.imprint","IMPRINT",FACE,{"disambiguationData":[TD([[makeQuery(id+"F6.imprint","IMPRINT",EDGE,{"derivedFrom":makeQuery(id+"F3.opExtrude","CAP_EDGE",EDGE,{"disambiguationData":[OSD([sQuery(id+"F2.wireOp",EDGE,"E21.MirrorCS")])],"isStart":true})}),1.0]])]});
            var Q20;
            {var subQ1=makeQuery(id+"F3.opExtrude","CAP_EDGE",EDGE,{"disambiguationData":[OSD([sQuery(id+"F2.wireOp",EDGE,"E15.MirrorCS")])],"isStart":true});Q20=makeQuery(id+"F6.imprint","IMPRINT",FACE,{"disambiguationData":[TD([[makeQuery(id+"F6.imprint","IMPRINT",EDGE,{"derivedFrom":subQ1}),1.0]])]});}
            var Q21;
            {var subQ0=makeQuery(id+"F3.opExtrude","CAP_EDGE",EDGE,{"disambiguationData":[OSD([sQuery(id+"F2.wireOp",EDGE,"E9.MirrorCS")])],"isStart":true});Q21=makeQuery(id+"F6.imprint","IMPRINT",FACE,{"disambiguationData":[TD([[makeQuery(id+"F6.imprint","IMPRINT",EDGE,{"derivedFrom":subQ0}),-1.0]])]});}
            var Q22;
            {var subQ1=makeQuery(id+"F3.opExtrude","CAP_EDGE",EDGE,{"disambiguationData":[OSD([sQuery(id+"F2.wireOp",EDGE,"E7.MirrorCS")])],"isStart":true});Q22=makeQuery(id+"F6.imprint","IMPRINT",FACE,{"disambiguationData":[TD([[makeQuery(id+"F6.imprint","IMPRINT",EDGE,{"derivedFrom":subQ1}),1.0]])]});}
            var Q23;
            {var subQ4=makeQuery(id+"F3.opExtrude","CAP_EDGE",EDGE,{"disambiguationData":[OSD([sQuery(id+"F2.wireOp",EDGE,"E28.MirrorCS")])],"isStart":true});Q23=makeQuery(id+"F6.imprint","IMPRINT",FACE,{"disambiguationData":[TD([[makeQuery(id+"F6.imprint","IMPRINT",EDGE,{"derivedFrom":subQ4}),1.0]])]});}
            var Q24;
            Q24=makeQuery(id+"F6.imprint","IMPRINT",FACE,{"disambiguationData":[TD([[makeQuery(id+"F6.imprint","IMPRINT",EDGE,{"derivedFrom":makeQuery(id+"F3.opExtrude","CAP_EDGE",EDGE,{"disambiguationData":[OSD([sQuery(id+"F2.wireOp",EDGE,"E4.top")])],"isStart":true})}),-1.0]])]});
            var Q25;
            Q25=makeQuery(id+"F6.imprint","IMPRINT",FACE,{"disambiguationData":[TD([[makeQuery(id+"F6.imprint","IMPRINT",EDGE,{"derivedFrom":makeQuery(id+"F3.opExtrude","CAP_EDGE",EDGE,{"disambiguationData":[OSD([sQuery(id+"F2.wireOp",EDGE,"E32.3.0.1")])],"isStart":true})}),-1.0]])]});
            var Q26;
            Q26=makeQuery(id+"F6.imprint","IMPRINT",FACE,{"disambiguationData":[TD([[makeQuery(id+"F6.imprint","IMPRINT",EDGE,{"derivedFrom":makeQuery(id+"F3.opExtrude","CAP_EDGE",EDGE,{"disambiguationData":[OSD([sQuery(id+"F2.wireOp",EDGE,"E32.1.0.1")])],"isStart":true})}),-1.0]])]});
            var Q27;
            Q27=makeQuery(id+"F6.imprint","IMPRINT",FACE,{"disambiguationData":[TD([[makeQuery(id+"F6.imprint","IMPRINT",EDGE,{"derivedFrom":makeQuery(id+"F3.opExtrude","CAP_EDGE",EDGE,{"disambiguationData":[OSD([sQuery(id+"F2.wireOp",EDGE,"E32.2.0.1")])],"isStart":true})}),-1.0]])]});
            var Q28;
            Q28=makeQuery(id+"F6.imprint","IMPRINT",FACE,{"disambiguationData":[TD([[makeQuery(id+"F6.imprint","IMPRINT",EDGE,{"derivedFrom":makeQuery(id+"F3.opExtrude","CAP_EDGE",EDGE,{"disambiguationData":[OSD([sQuery(id+"F2.wireOp",EDGE,"E32.4.0.1")])],"isStart":true})}),-1.0]])]});
            var Q29;
            Q29=makeQuery(id+"F6.imprint","IMPRINT",FACE,{"disambiguationData":[TD([[makeQuery(id+"F6.imprint","IMPRINT",EDGE,{"derivedFrom":makeQuery(id+"F3.opExtrude","CAP_EDGE",EDGE,{"disambiguationData":[OSD([sQuery(id+"F2.wireOp",EDGE,"E32.5.0.1")])],"isStart":true})}),-1.0]])]});
            var Q30;
            Q30=makeQuery(id+"F6.imprint","IMPRINT",FACE,{"disambiguationData":[TD([[makeQuery(id+"F6.imprint","IMPRINT",EDGE,{"derivedFrom":makeQuery(id+"F3.opExtrude","CAP_EDGE",EDGE,{"disambiguationData":[OSD([sQuery(id+"F2.wireOp",EDGE,"E32.6.0.1")])],"isStart":true})}),-1.0]])]});
            var Q31;
            Q31=makeQuery(id+"F6.imprint","IMPRINT",FACE,{"disambiguationData":[TD([[makeQuery(id+"F6.imprint","IMPRINT",EDGE,{"derivedFrom":makeQuery(id+"F3.opExtrude","CAP_EDGE",EDGE,{"disambiguationData":[OSD([sQuery(id+"F2.wireOp",EDGE,"E32.7.0.1")])],"isStart":true})}),-1.0]])]});
            var Q32;
            Q32=makeQuery(id+"F6.imprint","IMPRINT",FACE,{"disambiguationData":[TD([[makeQuery(id+"F6.imprint","IMPRINT",EDGE,{"derivedFrom":makeQuery(id+"F3.opExtrude","CAP_EDGE",EDGE,{"disambiguationData":[OSD([sQuery(id+"F2.wireOp",EDGE,"E32.8.0.1")])],"isStart":true})}),-1.0]])]});
            var Q33;
            Q33=makeQuery(id+"F6.imprint","IMPRINT",FACE,{"disambiguationData":[TD([[makeQuery(id+"F6.imprint","IMPRINT",EDGE,{"derivedFrom":makeQuery(id+"F3.opExtrude","CAP_EDGE",EDGE,{"disambiguationData":[OSD([sQuery(id+"F2.wireOp",EDGE,"E32.9.0.1")])],"isStart":true})}),-1.0]])]});
            var Q34;
            Q34=makeQuery(id+"F6.imprint","IMPRINT",FACE,{"disambiguationData":[TD([[makeQuery(id+"F6.imprint","IMPRINT",EDGE,{"derivedFrom":makeQuery(id+"F3.opExtrude","CAP_EDGE",EDGE,{"disambiguationData":[OSD([sQuery(id+"F2.wireOp",EDGE,"E32.10.0.1")])],"isStart":true})}),-1.0]])]});
            var Q35;
            Q35=makeQuery(id+"F6.imprint","IMPRINT",FACE,{"disambiguationData":[TD([[makeQuery(id+"F6.imprint","IMPRINT",EDGE,{"derivedFrom":makeQuery(id+"F3.opExtrude","CAP_EDGE",EDGE,{"disambiguationData":[OSD([sQuery(id+"F2.wireOp",EDGE,"E33.3.11.0")])],"isStart":true})}),-1.0]])]});
            var Q36;
            Q36=makeQuery(id+"F6.imprint","IMPRINT",FACE,{"disambiguationData":[TD([[makeQuery(id+"F6.imprint","IMPRINT",EDGE,{"derivedFrom":sQuery(id+"F6.wireOp",EDGE,"E90.0")}),1.0]])]});
            extrude(context, id + "F7", {"entities" : qUnion([Q0, Q1, Q2, Q3, Q4, Q5, Q6, Q7, Q8, Q9, Q10, Q11, Q12, Q13, Q14, Q15, Q16, Q17, Q18, Q19, Q20, Q21, Q22, Q23, Q24, Q25, Q26, Q27, Q28, Q29, Q30, Q31, Q32, Q33, Q34, Q35, Q36]), "operationType" : NewBodyOperationType.ADD, "depth" : 50.8 * mm});
        }
        {
            var Q0;
            Q0=makeQuery(id+"F1.opExtrude","SWEPT_FACE",FACE,{"disambiguationData":[OSD([sQuery(id+"F0.wireOp",EDGE,"E0.rect.left")])]});
            var sketch = newSketch(context, id + "F8", { "sketchPlane" : qUnion([Q0])});
            skLineSegment(sketch, "E93.0", {"start": v(-50.8, 55.56) * mm, "end": v(50.8, 55.56) * mm});
            skLineSegment(sketch, "E94", {"start": v(-57.15, 55.56) * mm, "end": v(57.15, 55.56) * mm});
            skLineSegment(sketch, "E95", {"start": v(0, 55.56) * mm, "end": v(0, 74.61) * mm, "construction": true});
            skPoint(sketch, "E95.endSnap0", {"position": v(0, 55.56) * mm});
            skLineSegment(sketch, "E96", {"start": v(-57.15, 55.56) * mm, "end": v(-57.15, 58.74) * mm});
            skLineSegment(sketch, "E97", {"start": v(57.15, 55.56) * mm, "end": v(57.15, 58.74) * mm});
            skLineSegment(sketch, "E98", {"start": v(-57.15, 58.74) * mm, "end": v(0, 74.61) * mm});
            skLineSegment(sketch, "E99", {"start": v(57.15, 58.74) * mm, "end": v(0, 74.61) * mm});
            skSolve(sketch);
        }
        {
            var Q0;
            {var subQ2=sQuery(id+"F8.wireOp",EDGE,"E96");Q0=makeQuery(id+"F8.imprint","IMPRINT",FACE,{"disambiguationData":[TD([[makeQuery(id+"F8.imprint","IMPRINT",EDGE,{"derivedFrom":subQ2}),-1.0]])]});}
            var Q1;
            Q1 = qConstructionFilter(qBodyType(qCreatedBy(id + "F8" ,EDGE), BodyType.WIRE), ConstructionObject.NO);
            var Q2;
            Q2=makeQuery(id+"F1.opExtrude","SWEPT_FACE",FACE,{"disambiguationData":[OSD([sQuery(id+"F0.wireOp",EDGE,"E0.rect.right")])]});
            extrude(context, id + "F9", {"entities" : qUnion([Q0]), "operationType" : NewBodyOperationType.ADD, "surfaceEntities" : qUnion([Q1]), "endBound" : BoundingType.UP_TO_SURFACE, "oppositeDirection" : true, "endBoundEntityFace" : qUnion([Q2]), "depth" : 25.4 * mm});
        }
    });
